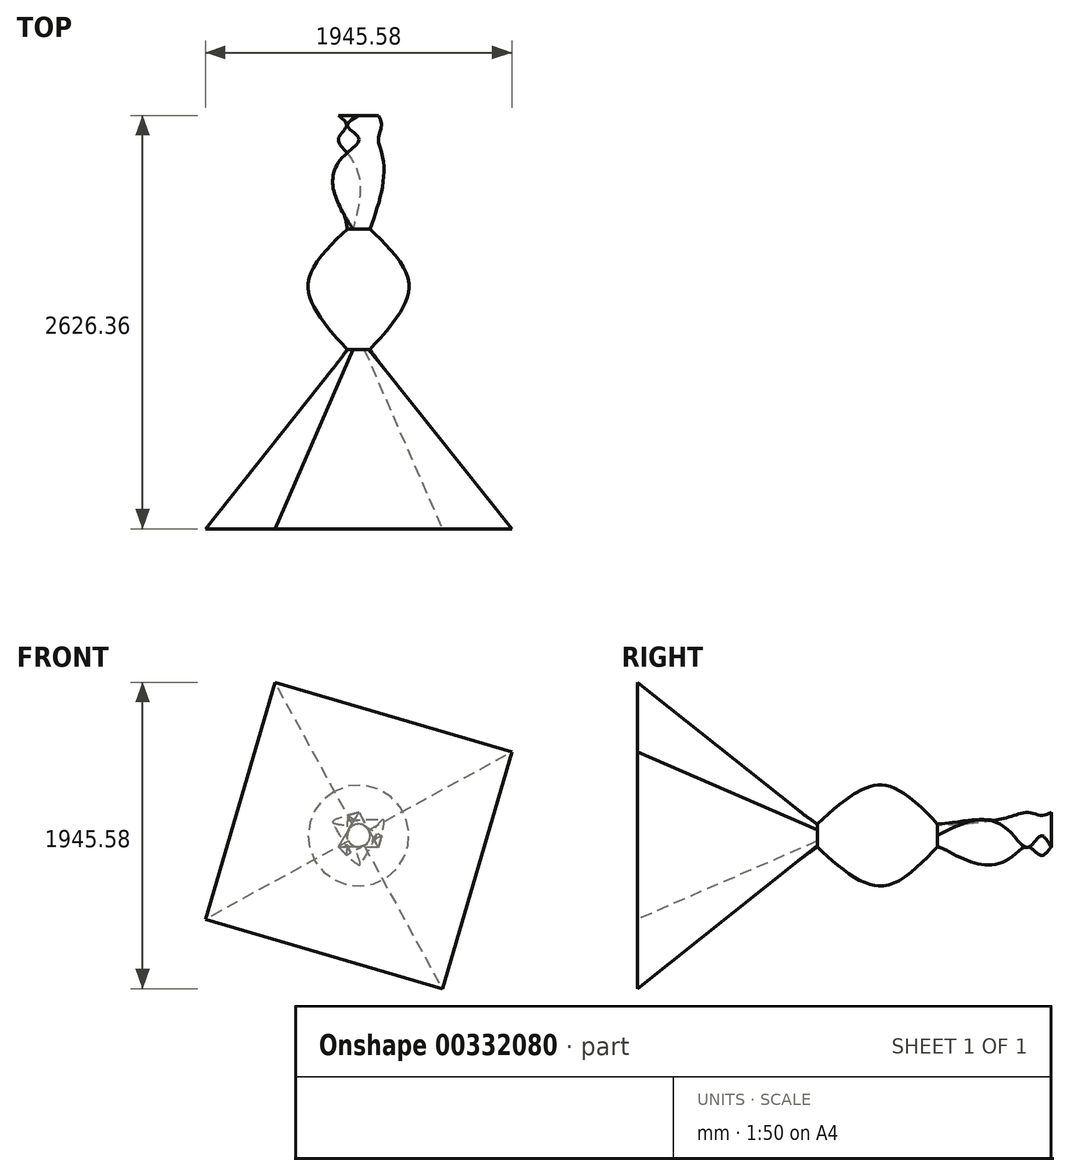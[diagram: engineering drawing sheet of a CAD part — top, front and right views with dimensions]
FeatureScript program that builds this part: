
annotation { "Feature Type Name" : "Feature", "Feature Type Description" : "" }
export const myFeature = defineFeature(function(context is Context, id is Id, definition is map)
    precondition{}
    {
        {
            var Q0;
            Q0=qCreatedBy(makeId("Front.planeOp"),FACE);
            cPlane(context, id + "F0", {"entities" : qUnion([Q0]), "cplaneType" : CPlaneType.OFFSET, "offset" : 60.96 * mm, "width" : 152.4 * mm, "height" : 152.4 * mm});
        }
        {
            var Q0;
            Q0=qCreatedBy(id+"F0.planeOp",FACE);
            cPlane(context, id + "F1", {"entities" : qUnion([Q0]), "cplaneType" : CPlaneType.OFFSET, "offset" : 81.28 * mm, "width" : 152.4 * mm, "height" : 152.4 * mm});
        }
        {
            var Q0;
            Q0=qCreatedBy(id+"F1.planeOp",FACE);
            cPlane(context, id + "F2", {"entities" : qUnion([Q0]), "cplaneType" : CPlaneType.OFFSET, "offset" : 96.52 * mm, "width" : 152.4 * mm, "height" : 152.4 * mm});
        }
        {
            var Q0;
            Q0=qCreatedBy(id+"F2.planeOp",FACE);
            cPlane(context, id + "F3", {"entities" : qUnion([Q0]), "cplaneType" : CPlaneType.OFFSET, "offset" : 482.6 * mm, "width" : 152.4 * mm, "height" : 152.4 * mm});
        }
        {
            var Q0;
            Q0=qCreatedBy(makeId("Front.planeOp"),FACE);
            var sketch = newSketch(context, id + "F4", { "sketchPlane" : qUnion([Q0])});
            skCircle(sketch, "E0.cCircle", {"center": v(0, 0) * mm, "radius": 73.32 * mm, "construction": true});
            skLineSegment(sketch, "E0.0", {"start": v(-128.16, -71.29) * mm, "end": v(2.34, 146.63) * mm});
            skLineSegment(sketch, "E0.1", {"start": v(2.34, 146.63) * mm, "end": v(125.81, -75.34) * mm});
            skLineSegment(sketch, "E0.2", {"start": v(125.81, -75.34) * mm, "end": v(-128.16, -71.29) * mm});
            skPoint(sketch, "E0.0.midPoint", {"position": v(-62.9, 37.67) * mm});
            skSolve(sketch);
        }
        {
            var Q0;
            Q0=qCreatedBy(id+"F0.planeOp",FACE);
            var sketch = newSketch(context, id + "F5", { "sketchPlane" : qUnion([Q0])});
            skCircle(sketch, "E1.cCircle", {"center": v(0, 0) * mm, "radius": 73.32 * mm, "construction": true});
            skLineSegment(sketch, "E1.0", {"start": v(146.63, -2.54) * mm, "end": v(-75.51, -125.71) * mm});
            skLineSegment(sketch, "E1.1", {"start": v(-75.51, -125.71) * mm, "end": v(-71.11, 128.25) * mm});
            skLineSegment(sketch, "E1.2", {"start": v(-71.11, 128.25) * mm, "end": v(146.63, -2.54) * mm});
            skPoint(sketch, "E1.0.midPoint", {"position": v(35.56, -64.12) * mm});
            skSolve(sketch);
        }
        {
            var Q0;
            Q0=qCreatedBy(id+"F1.planeOp",FACE);
            var sketch = newSketch(context, id + "F6", { "sketchPlane" : qUnion([Q0])});
            skCircle(sketch, "E2.cCircle", {"center": v(0, 0) * mm, "radius": 73.32 * mm, "construction": true});
            skLineSegment(sketch, "E2.0", {"start": v(127, -73.32) * mm, "end": v(-127, -73.32) * mm});
            skLineSegment(sketch, "E2.1", {"start": v(-127, -73.32) * mm, "end": v(0, 146.65) * mm});
            skLineSegment(sketch, "E2.2", {"start": v(0, 146.65) * mm, "end": v(127, -73.32) * mm});
            skPoint(sketch, "E2.0.midPoint", {"position": v(0, -73.32) * mm});
            skSolve(sketch);
        }
        {
            var Q0;
            Q0=qCreatedBy(id+"F2.planeOp",FACE);
            var sketch = newSketch(context, id + "F7", { "sketchPlane" : qUnion([Q0])});
            skCircle(sketch, "E3.cCircle", {"center": v(0, 0) * mm, "radius": 73.32 * mm, "construction": true});
            skLineSegment(sketch, "E3.0", {"start": v(146.65, 0.18) * mm, "end": v(-73.17, -127.09) * mm});
            skLineSegment(sketch, "E3.1", {"start": v(-73.17, -127.09) * mm, "end": v(-73.48, 126.91) * mm});
            skLineSegment(sketch, "E3.2", {"start": v(-73.48, 126.91) * mm, "end": v(146.65, 0.18) * mm});
            skPoint(sketch, "E3.0.midPoint", {"position": v(36.74, -63.46) * mm});
            skSolve(sketch);
        }
        {
            var Q0;
            Q0=qCreatedBy(id+"F3.planeOp",FACE);
            var sketch = newSketch(context, id + "F8", { "sketchPlane" : qUnion([Q0])});
            skCircle(sketch, "E4", {"center": v(0, 0) * mm, "radius": 73.1 * mm});
            skSolve(sketch);
        }
        {
            var Q0;
            Q0=makeQuery(id+"F4.imprint","IMPRINT",FACE,{"disambiguationData":[TD([[makeQuery(id+"F4.imprint","IMPRINT",EDGE,{"derivedFrom":sQuery(id+"F4.wireOp",EDGE,"E0.0")}),-1.0]])]});
            var Q1;
            Q1=makeQuery(id+"F5.imprint","IMPRINT",FACE,{"disambiguationData":[TD([[makeQuery(id+"F5.imprint","IMPRINT",EDGE,{"derivedFrom":sQuery(id+"F5.wireOp",EDGE,"E1.0")}),-1.0]])]});
            var Q2;
            Q2=makeQuery(id+"F6.imprint","IMPRINT",FACE,{"disambiguationData":[TD([[makeQuery(id+"F6.imprint","IMPRINT",EDGE,{"derivedFrom":sQuery(id+"F6.wireOp",EDGE,"E2.0")}),-1.0]])]});
            var Q3;
            Q3=makeQuery(id+"F7.imprint","IMPRINT",FACE,{"disambiguationData":[TD([[makeQuery(id+"F7.imprint","IMPRINT",EDGE,{"derivedFrom":sQuery(id+"F7.wireOp",EDGE,"E3.0")}),-1.0]])]});
            var Q4;
            Q4=makeQuery(id+"F8.imprint","IMPRINT",FACE,{"disambiguationData":[TD([[makeQuery(id+"F8.imprint","IMPRINT",EDGE,{"derivedFrom":sQuery(id+"F8.wireOp",EDGE,"E4")}),1.0]])]});
            loft(context, id + "F9", {"sheetProfilesArray" : [{ "sheetProfileEntities" : qUnion([Q0]) }, { "sheetProfileEntities" : qUnion([Q1]) }, { "sheetProfileEntities" : qUnion([Q2]) }, { "sheetProfileEntities" : qUnion([Q3]) }, { "sheetProfileEntities" : qUnion([Q4]) }]});
        }
        {
            var Q0;
            Q0=qCreatedBy(id+"F3.planeOp",FACE);
            cPlane(context, id + "F10", {"entities" : qUnion([Q0]), "cplaneType" : CPlaneType.OFFSET, "offset" : 347.98 * mm, "width" : 152.4 * mm, "height" : 152.4 * mm});
        }
        {
            var Q0;
            Q0=qCreatedBy(id+"F10.planeOp",FACE);
            cPlane(context, id + "F11", {"entities" : qUnion([Q0]), "cplaneType" : CPlaneType.OFFSET, "offset" : 416.56 * mm, "width" : 152.4 * mm, "height" : 152.4 * mm});
        }
        {
            var Q0;
            Q0=qCreatedBy(id+"F3.planeOp",FACE);
            var sketch = newSketch(context, id + "F12", { "sketchPlane" : qUnion([Q0])});
            skCircle(sketch, "E5", {"center": v(0, 0) * mm, "radius": 71.72 * mm});
            skSolve(sketch);
        }
        {
            var Q0;
            Q0=qCreatedBy(id+"F10.planeOp",FACE);
            var sketch = newSketch(context, id + "F13", { "sketchPlane" : qUnion([Q0])});
            skCircle(sketch, "E6", {"center": v(0, 0) * mm, "radius": 320.09 * mm});
            skSolve(sketch);
        }
        {
            var Q0;
            Q0=qCreatedBy(id+"F11.planeOp",FACE);
            var sketch = newSketch(context, id + "F14", { "sketchPlane" : qUnion([Q0])});
            skCircle(sketch, "E7", {"center": v(0, 0) * mm, "radius": 73.16 * mm});
            skSolve(sketch);
        }
        {
            var Q1;
            Q1=makeQuery(id+"F12.imprint","IMPRINT",FACE,{"disambiguationData":[TD([[makeQuery(id+"F12.imprint","IMPRINT",EDGE,{"derivedFrom":sQuery(id+"F12.wireOp",EDGE,"E5")}),1.0]])]});
            var Q2;
            Q2=makeQuery(id+"F13.imprint","IMPRINT",FACE,{"disambiguationData":[TD([[makeQuery(id+"F13.imprint","IMPRINT",EDGE,{"derivedFrom":sQuery(id+"F13.wireOp",EDGE,"E6")}),1.0]])]});
            var Q3;
            Q3=makeQuery(id+"F14.imprint","IMPRINT",FACE,{"disambiguationData":[TD([[makeQuery(id+"F14.imprint","IMPRINT",EDGE,{"derivedFrom":sQuery(id+"F14.wireOp",EDGE,"E7")}),1.0]])]});
            loft(context, id + "F15", {"operationType" : NewBodyOperationType.ADD, "sheetProfilesArray" : [{ "sheetProfileEntities" : qUnion([Q1]) }, { "sheetProfileEntities" : qUnion([Q2]) }, { "sheetProfileEntities" : qUnion([Q3]) }]});
        }
        {
            var Q0;
            Q0=qCreatedBy(id+"F11.planeOp",FACE);
            cPlane(context, id + "F16", {"entities" : qUnion([Q0]), "cplaneType" : CPlaneType.OFFSET, "offset" : 1140.46 * mm, "width" : 152.4 * mm, "height" : 152.4 * mm});
        }
        {
            var Q0;
            Q0=qCreatedBy(id+"F16.planeOp",FACE);
            var sketch = newSketch(context, id + "F17", { "sketchPlane" : qUnion([Q0])});
            skCircle(sketch, "E8.cCircle", {"center": v(0, 0) * mm, "radius": 783.85 * mm, "construction": true});
            skLineSegment(sketch, "E8.0", {"start": v(972.8, 531.53) * mm, "end": v(531.53, -972.8) * mm});
            skLineSegment(sketch, "E8.1", {"start": v(531.53, -972.8) * mm, "end": v(-972.8, -531.53) * mm});
            skLineSegment(sketch, "E8.2", {"start": v(-972.8, -531.53) * mm, "end": v(-531.53, 972.8) * mm});
            skLineSegment(sketch, "E8.3", {"start": v(-531.53, 972.8) * mm, "end": v(972.8, 531.53) * mm});
            skPoint(sketch, "E8.0.midPoint", {"position": v(752.16, -220.63) * mm});
            skSolve(sketch);
        }
        {
            var Q1;
            Q1=makeQuery(id+"F15.opLoft","CAP_FACE",FACE,{"disambiguationData":[OSD([makeQuery(id+"F14.imprint","IMPRINT",FACE,{"disambiguationData":[TD([[makeQuery(id+"F14.imprint","IMPRINT",EDGE,{"derivedFrom":sQuery(id+"F14.wireOp",EDGE,"E7")}),1.0]])]})])],"isStart":true});
            var Q2;
            Q2=makeQuery(id+"F17.imprint","IMPRINT",FACE,{"disambiguationData":[TD([[makeQuery(id+"F17.imprint","IMPRINT",EDGE,{"derivedFrom":sQuery(id+"F17.wireOp",EDGE,"E8.0")}),-1.0]])]});
            loft(context, id + "F18", {"operationType" : NewBodyOperationType.ADD, "sheetProfilesArray" : [{ "sheetProfileEntities" : qUnion([Q1]) }, { "sheetProfileEntities" : qUnion([Q2]) }]});
        }
    });
